# Revit family: 591_XOX_nailfin
name_source: partatom
category: Windows
revit_build: Autodesk Revit 2016 (Build: 20150220_1215(x64)
units: mm (PartAtom-declared; Revit-internal decimal feet)

## family parameters
Always vertical = Yes
Cut with Voids When Loaded = No
Host = Wall
OmniClass Number = 23.30.20.00
OmniClass Title = Windows
Room Calculation Point = No
Shared = No

## types (94) — shared parameters
Default Sill Height = 31 1/2"
Wall Closure = By host

## per-type parameters (varying)
| type | BSL | BSR | Height | MLW | Width |
| 72x24 | 18" | 18" | 24" | 4 1/2" | 72" |
| 108x36 | 27" | 27" | 36" | 6 3/4" | 108" |
| 36x12Min | 12" | 12" | 12" | 3" | 36" |
| 108x66Max | 27" | 27" | 66" | 6 3/4" | 108" |
| 48x24 | 12" | 12" | 24" | 3" | 48" |
| 60x30 | 15" | 15" | 30" | 3 3/4" | 60" |
| 84x36 | 21" | 21" | 36" | 5 1/4" | 84" |
| 96x36 | 24" | 24" | 36" | 6" | 96" |
| 36x18 | 12" | 12" | 18" | 3" | 36" |
| 36x24 | 12" | 12" | 24" | 3" | 36" |
| 42x12 | 12" | 12" | 12" | 3" | 42" |
| 42x18 | 12" | 12" | 18" | 3" | 42" |
| 42x24 | 12" | 12" | 24" | 3" | 42" |
| 42x30 | 12" | 12" | 30" | 3" | 42" |
| 48x12 | 12" | 12" | 12" | 3" | 48" |
| 48x18 | 12" | 12" | 18" | 3" | 48" |
| 48x30 | 12" | 12" | 30" | 3" | 48" |
| 48x36 | 12" | 12" | 36" | 3" | 48" |
| 48x42 | 12" | 12" | 42" | 3" | 48" |
| 54x48 | 13 1/2" | 13 1/2" | 48" | 3 3/8" | 54" |
| 54x18 | 13 1/2" | 13 1/2" | 18" | 3 3/8" | 54" |
| 54x24 | 13 1/2" | 13 1/2" | 24" | 3 3/8" | 54" |
| 54x30 | 13 1/2" | 13 1/2" | 30" | 3 3/8" | 54" |
| 54x36 | 13 1/2" | 13 1/2" | 36" | 3 3/8" | 54" |
| 54x42 | 13 1/2" | 13 1/2" | 42" | 3 3/8" | 54" |
| 54x54 | 13 1/2" | 13 1/2" | 54" | 3 3/8" | 54" |
| 54x60 | 13 1/2" | 13 1/2" | 60" | 3 3/8" | 54" |
| 48x48 | 12" | 12" | 48" | 3" | 48" |
| 60x24 | 15" | 15" | 24" | 3 3/4" | 60" |
| 60x18 | 15" | 15" | 18" | 3 3/4" | 60" |
| 60x36 | 15" | 15" | 36" | 3 3/4" | 60" |
| 60x42 | 15" | 15" | 42" | 3 3/4" | 60" |
| 60x48 | 15" | 15" | 48" | 3 3/4" | 60" |
| 60x54 | 15" | 15" | 54" | 3 3/4" | 60" |
| 60x60 | 15" | 15" | 60" | 3 3/4" | 60" |
| 60x66 | 15" | 15" | 66" | 3 3/4" | 60" |
| 66x30 | 16 1/2" | 16 1/2" | 30" | 4 1/8" | 66" |
| 66x24 | 16 1/2" | 16 1/2" | 24" | 4 1/8" | 66" |
| 66x18 | 16 1/2" | 16 1/2" | 18" | 4 1/8" | 66" |
| 66x36 | 16 1/2" | 16 1/2" | 36" | 4 1/8" | 66" |
| 66x42 | 16 1/2" | 16 1/2" | 42" | 4 1/8" | 66" |
| 66x48 | 16 1/2" | 16 1/2" | 48" | 4 1/8" | 66" |
| 66x54 | 16 1/2" | 16 1/2" | 54" | 4 1/8" | 66" |
| 66x60 | 16 1/2" | 16 1/2" | 60" | 4 1/8" | 66" |
| 66x66 | 16 1/2" | 16 1/2" | 66" | 4 1/8" | 66" |
| 72x30 | 18" | 18" | 30" | 4 1/2" | 72" |
| 72x36 | 18" | 18" | 36" | 4 1/2" | 72" |
| 72x42 | 18" | 18" | 42" | 4 1/2" | 72" |
| 72x48 | 18" | 18" | 48" | 4 1/2" | 72" |
| 72x54 | 18" | 18" | 54" | 4 1/2" | 72" |
| 72x60 | 18" | 18" | 60" | 4 1/2" | 72" |
| 72x66 | 18" | 18" | 66" | 4 1/2" | 72" |
| 78x24 | 19 1/2" | 19 1/2" | 24" | 4 7/8" | 78" |
| 78x30 | 19 1/2" | 19 1/2" | 30" | 4 7/8" | 78" |
| 78x36 | 19 1/2" | 19 1/2" | 36" | 4 7/8" | 78" |
| 78x42 | 19 1/2" | 19 1/2" | 42" | 4 7/8" | 78" |
| 78x48 | 19 1/2" | 19 1/2" | 48" | 4 7/8" | 78" |
| 78x54 | 19 1/2" | 19 1/2" | 54" | 4 7/8" | 78" |
| 78x60 | 19 1/2" | 19 1/2" | 60" | 4 7/8" | 78" |
| 78x66 | 19 1/2" | 19 1/2" | 66" | 4 7/8" | 78" |
| 84x24 | 21" | 21" | 24" | 5 1/4" | 84" |
| 84x30 | 21" | 21" | 30" | 5 1/4" | 84" |
| 84x42 | 21" | 21" | 42" | 5 1/4" | 84" |
| 84x48 | 21" | 21" | 48" | 5 1/4" | 84" |
| 84x54 | 21" | 21" | 54" | 5 1/4" | 84" |
| 84x60 | 21" | 21" | 60" | 5 1/4" | 84" |
| 84x66 | 21" | 21" | 66" | 5 1/4" | 84" |
| 90x24 | 22 1/2" | 22 1/2" | 24" | 5 5/8" | 90" |
| 90x30 | 22 1/2" | 22 1/2" | 30" | 5 5/8" | 90" |
| 90x36 | 22 1/2" | 22 1/2" | 36" | 5 5/8" | 90" |
| 90x42 | 22 1/2" | 22 1/2" | 42" | 5 5/8" | 90" |
| 90x48 | 22 1/2" | 22 1/2" | 48" | 5 5/8" | 90" |
| 90x54 | 22 1/2" | 22 1/2" | 54" | 5 5/8" | 90" |
| 90x60 | 22 1/2" | 22 1/2" | 60" | 5 5/8" | 90" |
| 90x66 | 22 1/2" | 22 1/2" | 66" | 5 5/8" | 90" |
| 96x30 | 24" | 24" | 30" | 6" | 96" |
| 96x24 | 24" | 24" | 24" | 6" | 96" |
| 96x42 | 24" | 24" | 42" | 6" | 96" |
| 96x48 | 24" | 24" | 48" | 6" | 96" |
| 96x54 | 24" | 24" | 54" | 6" | 96" |
| 96x60 | 24" | 24" | 60" | 6" | 96" |
| 96x66 | 24" | 24" | 66" | 6" | 96" |
| 102x30 | 25 1/2" | 25 1/2" | 30" | 6 3/8" | 102" |
| 102x36 | 25 1/2" | 25 1/2" | 36" | 6 3/8" | 102" |
| 102x42 | 25 1/2" | 25 1/2" | 42" | 6 3/8" | 102" |
| 102x48 | 25 1/2" | 25 1/2" | 48" | 6 3/8" | 102" |
| 102x54 | 25 1/2" | 25 1/2" | 54" | 6 3/8" | 102" |
| 102x60 | 25 1/2" | 25 1/2" | 60" | 6 3/8" | 102" |
| 102x66 | 25 1/2" | 25 1/2" | 66" | 6 3/8" | 102" |
| 108x30 | 27" | 27" | 30" | 6 3/4" | 108" |
| 108x42 | 27" | 27" | 42" | 6 3/4" | 108" |
| 108x48 | 27" | 27" | 48" | 6 3/4" | 108" |
| 108x54 | 27" | 27" | 54" | 6 3/4" | 108" |
| 108x60 | 27" | 27" | 60" | 6 3/4" | 108" |

## geometry (parser evidence)
native form markers: Sweep x3
no freeform markers — native parametric forms only
